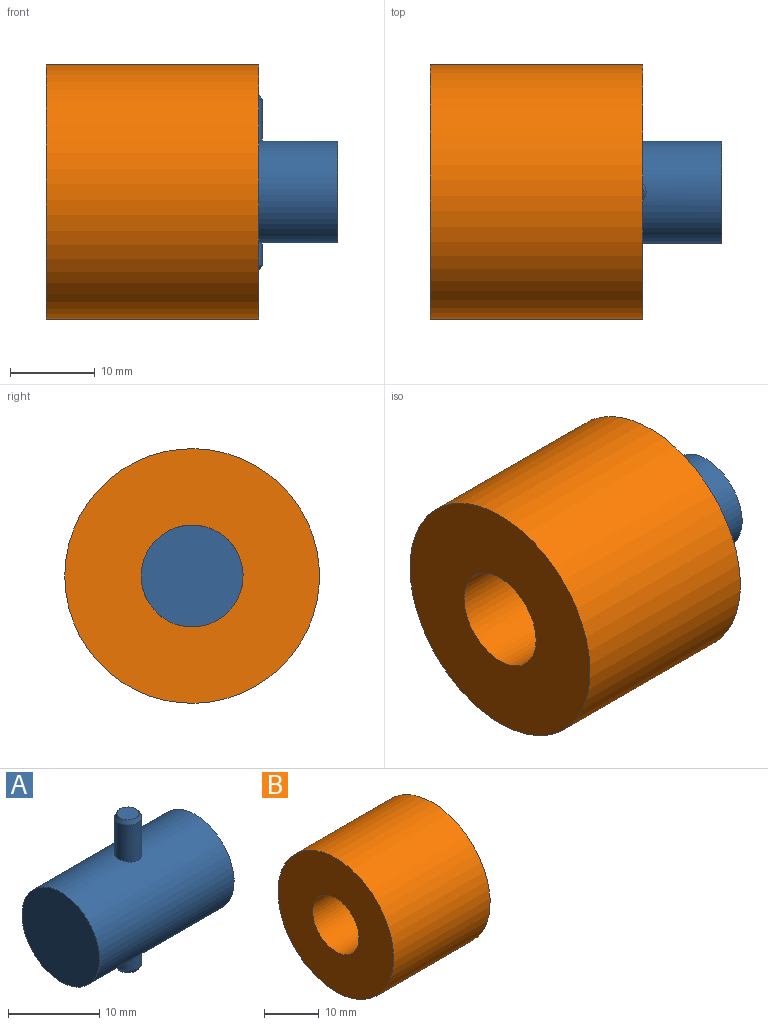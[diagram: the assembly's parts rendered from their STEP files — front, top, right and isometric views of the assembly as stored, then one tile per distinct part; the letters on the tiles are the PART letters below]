
ASSEMBLY  parts=2 mates=1
PART A: 9 faces, bbox 20.8x12x20.5 mm
  f0: cylinder r=6mm len=20.8mm, axis (-1,0,0), area 770mm2, adj f1,f2,f5,f6
  f1: plane 12x12mm, normal (1,0,0), area 113.1mm2, adj f0
  f2: plane 12x12mm, normal (-1,0,0), area 113.1mm2, adj f0
  f3: plane 2.42x2.42mm, normal (0,0,1), area 4.6mm2, adj f4
  f4: cone r=1.5mm half-angle=30deg, axis (0,0,-1), area 4.9mm2, adj f3,f5
  f5: cylinder r=1.5mm len=4.86mm, axis (0,0,1), area 45.8mm2, adj f0,f4
  f6: cylinder r=1.5mm len=3mm, axis (0,0,1), area 24.9mm2, adj f0,f8
  f7: plane 2.42x2.42mm, normal (0,0,-1), area 4.6mm2, adj f8
  f8: cone r=1.21mm half-angle=30deg, axis (0,0,1), area 4.9mm2, adj f6,f7
PART B: 18 faces, bbox 25x30x30 mm
  f0: cylinder r=6mm len=25mm, axis (1,0,0), area 910.9mm2, adj f2,f3,f5,f6,f7,f8,f9,f10
  f1: cylinder r=14.98mm len=29.97mm, axis (1,0,0), area 2353.8mm2, adj f2,f3
  f2: plane 29.97x29.97mm, normal (-1,0,0), area 592.3mm2, adj f0,f1
  f3: plane 29.97x29.97mm, normal (1,0,0), area 556.5mm2, adj f0,f1,f4,f6,f7,f9,f10,f11
  f4: cylinder r=1.51mm len=4mm, axis (1,0,0), area 19mm2, adj f3,f6,f7,f16
  f5: plane 3.9x0.02mm, normal (1,0,0), area 0.1mm2, adj f0,f15,f16,f17
  f6: plane 4.08x4mm, normal (0,1,0), area 16.3mm2, adj f0,f3,f4,f17
  f7: plane 4.08x4mm, normal (0,-1,0), area 16.3mm2, adj f0,f3,f4,f15
  f8: plane 5.5x0.02mm, normal (1,0,0), area 0.1mm2, adj f0,f12,f13,f14
  f9: plane 5.68x4mm, normal (0,-1,0), area 22.7mm2, adj f0,f3,f11,f12
  f10: plane 5.68x4mm, normal (0,1,0), area 22.7mm2, adj f0,f3,f11,f14
  f11: cylinder r=1.51mm len=4mm, axis (1,0,0), area 19mm2, adj f3,f9,f10,f13
  f12: cylinder r=1.5mm len=5.68mm, axis (0,0,1), area 13.2mm2, adj f0,f8,f9,f13
  f13: torus R=0.01mm, axis (1,0,0), area 7.1mm2, adj f8,f11,f12,f14
  f14: cylinder r=1.5mm len=5.68mm, axis (0,0,-1), area 13.2mm2, adj f0,f8,f10,f13
  f15: cylinder r=1.5mm len=4.08mm, axis (0,0,1), area 9.4mm2, adj f0,f5,f7,f16
  f16: torus R=0.01mm, axis (1,0,0), area 7.1mm2, adj f4,f5,f15,f17
  f17: cylinder r=1.5mm len=4.08mm, axis (0,0,-1), area 9.4mm2, adj f0,f5,f6,f16
PLACE A t=(11.25,-4.81,4.58)mm
PLACE B t=(12.37,-4.81,4.58)mm
MATE cylindrical A.f0 <-> B.f0  axis (-1,0,0) through (11.25,-4.81,4.58)mm
